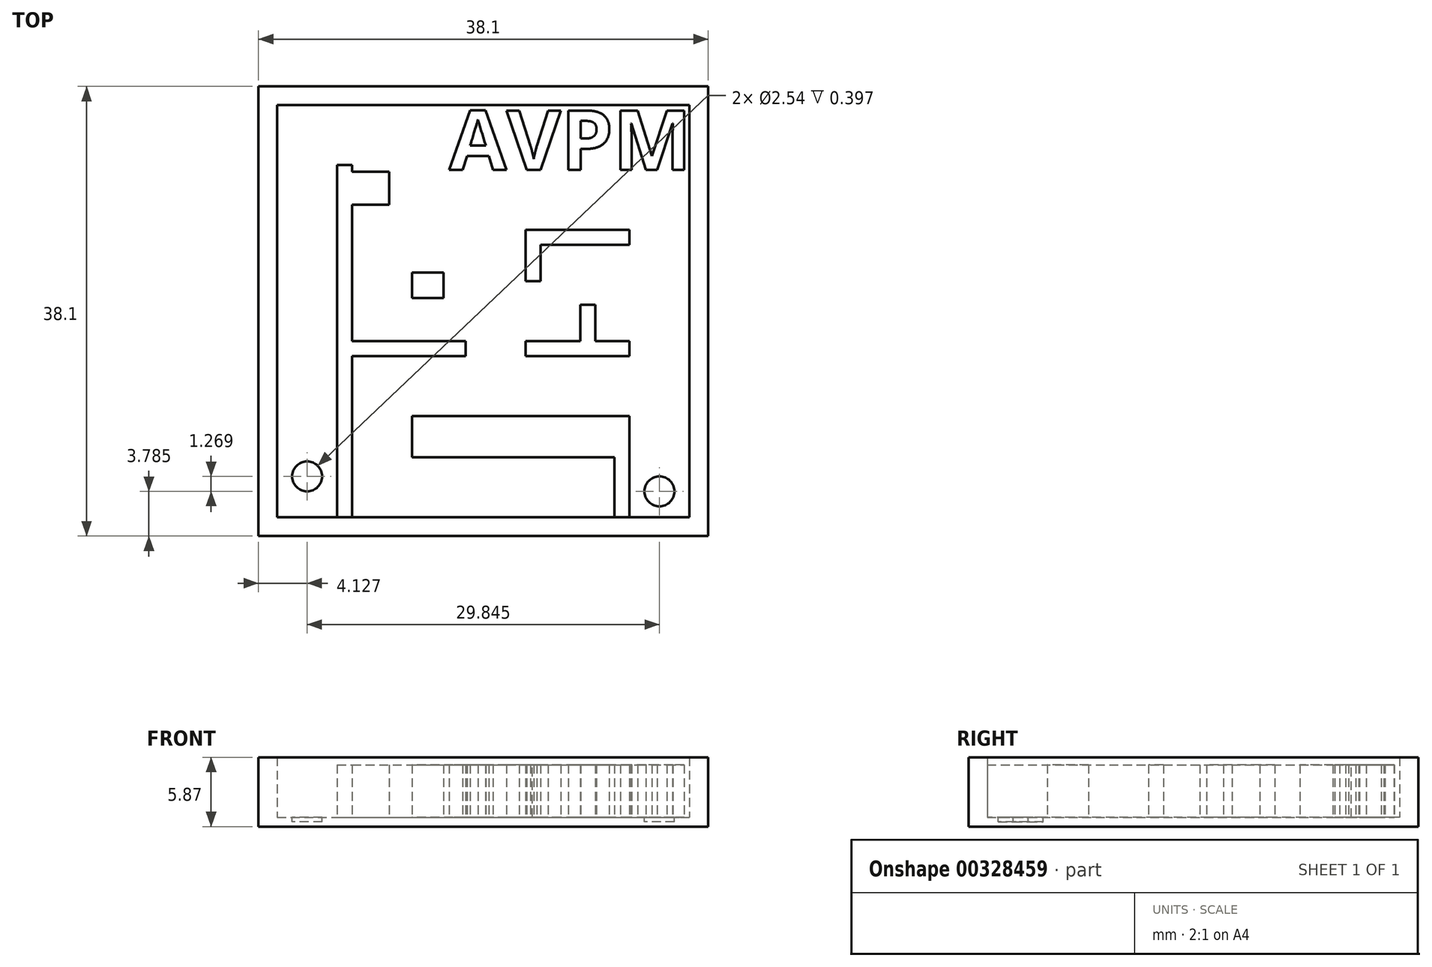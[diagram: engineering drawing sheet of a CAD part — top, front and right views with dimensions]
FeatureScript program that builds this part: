
annotation { "Feature Type Name" : "Feature", "Feature Type Description" : "" }
export const myFeature = defineFeature(function(context is Context, id is Id, definition is map)
    precondition{}
    {
        {
            var Q0;
            Q0=qCreatedBy(makeId("Top.planeOp"),FACE);
            var sketch = newSketch(context, id + "F0", { "sketchPlane" : qUnion([Q0])});
            skLineSegment(sketch, "E0.bottom", {"start": v(-17.86, 15.09) * mm, "end": v(20.24, 15.09) * mm});
            skLineSegment(sketch, "E0.top", {"start": v(-17.86, -23.01) * mm, "end": v(20.24, -23.01) * mm});
            skLineSegment(sketch, "E0.left", {"start": v(-17.86, 15.09) * mm, "end": v(-17.86, -23.01) * mm});
            skLineSegment(sketch, "E0.right", {"start": v(20.24, 15.09) * mm, "end": v(20.24, -23.01) * mm});
            skSolve(sketch);
        }
        {
            var Q0;
            Q0=makeQuery(id+"F0.imprint","IMPRINT",FACE,{"disambiguationData":[TD([[makeQuery(id+"F0.imprint","IMPRINT",EDGE,{"derivedFrom":sQuery(id+"F0.wireOp",EDGE,"E0.bottom")}),-1.0]])]});
            extrude(context, id + "F1", {"entities" : qUnion([Q0]), "depth" : 0.8 * mm});
        }
        {
            var Q0;
            Q0=makeQuery(id+"F1.opExtrude","CAP_FACE",FACE,{"disambiguationData":[OSD([sQuery(id+"F0.wireOp",EDGE,"E0.bottom"),sQuery(id+"F0.wireOp",EDGE,"E0.top"),sQuery(id+"F0.wireOp",EDGE,"E0.left"),sQuery(id+"F0.wireOp",EDGE,"E0.right")])],"isStart":false});
            var sketch = newSketch(context, id + "F2", { "sketchPlane" : qUnion([Q0])});
            skLineSegment(sketch, "E1.0", {"start": v(-16.27, 13.5) * mm, "end": v(18.65, 13.5) * mm});
            skLineSegment(sketch, "E1.1", {"start": v(-16.27, 13.5) * mm, "end": v(-16.27, -21.43) * mm});
            skLineSegment(sketch, "E1.2", {"start": v(-16.27, -21.43) * mm, "end": v(18.65, -21.43) * mm});
            skLineSegment(sketch, "E1.3", {"start": v(18.65, 13.5) * mm, "end": v(18.65, -21.43) * mm});
            skSolve(sketch);
        }
        {
            var Q0;
            Q0=makeQuery(id+"F2.imprint","IMPRINT",FACE,{"disambiguationData":[TD([[makeQuery(id+"F2.imprint","IMPRINT",EDGE,{"derivedFrom":sQuery(id+"F2.wireOp",EDGE,"E1.0")}),1.0]])]});
            extrude(context, id + "F3", {"entities" : qUnion([Q0]), "operationType" : NewBodyOperationType.ADD, "depth" : 5.08 * mm});
        }
        {
            var Q0;
            Q0=makeQuery(id+"F1.opExtrude","CAP_FACE",FACE,{"disambiguationData":[OSD([sQuery(id+"F0.wireOp",EDGE,"E0.bottom"),sQuery(id+"F0.wireOp",EDGE,"E0.top"),sQuery(id+"F0.wireOp",EDGE,"E0.left"),sQuery(id+"F0.wireOp",EDGE,"E0.right")])],"isStart":false});
            var sketch = newSketch(context, id + "F4", { "sketchPlane" : qUnion([Q0])});
            skLineSegment(sketch, "E2.bottom", {"start": v(-11.2, -21.43) * mm, "end": v(-9.92, -21.43) * mm});
            skLineSegment(sketch, "E2.top", {"start": v(-11.2, 8.42) * mm, "end": v(-9.92, 8.42) * mm});
            skLineSegment(sketch, "E2.left", {"start": v(-11.2, -21.43) * mm, "end": v(-11.2, 8.42) * mm});
            skLineSegment(sketch, "E2.right", {"start": v(-9.92, -21.43) * mm, "end": v(-9.92, -7.77) * mm});
            skLineSegment(sketch, "E3.bottom", {"start": v(12.3, -21.43) * mm, "end": v(13.57, -21.43) * mm});
            skLineSegment(sketch, "E3.left", {"start": v(12.3, -21.43) * mm, "end": v(12.3, -16.35) * mm});
            skLineSegment(sketch, "E3.right", {"start": v(13.57, -21.43) * mm, "end": v(13.57, -16.35) * mm});
            skLineSegment(sketch, "E4.bottom", {"start": v(-4.84, -12.85) * mm, "end": v(12.3, -12.85) * mm});
            skLineSegment(sketch, "E4.left", {"start": v(-4.84, -12.85) * mm, "end": v(-4.84, -16.35) * mm});
            skLineSegment(sketch, "E5.right", {"start": v(-0.7, -16.2) * mm, "end": v(-0.7, -16.35) * mm});
            skLineSegment(sketch, "E6.bottom", {"start": v(-9.92, -6.5) * mm, "end": v(-0.3, -6.5) * mm});
            skLineSegment(sketch, "E6.top", {"start": v(-9.92, -7.77) * mm, "end": v(-0.3, -7.77) * mm});
            skLineSegment(sketch, "E6.right", {"start": v(-0.3, -6.5) * mm, "end": v(-0.3, -7.77) * mm});
            skLineSegment(sketch, "E7", {"start": v(-4.84, -16.35) * mm, "end": v(12.3, -16.35) * mm});
            skLineSegment(sketch, "E8.trimOffspring", {"start": v(-9.92, -6.5) * mm, "end": v(-9.92, 5.05) * mm});
            skPoint(sketch, "E9.bottom.end.orphan", {"position": v(0.9, 4.03) * mm});
            skPoint(sketch, "E10.right.end.orphan", {"position": v(-4.84, -1.05) * mm});
            skPoint(sketch, "E11.trimOffspring.start.orphan", {"position": v(0.9, -2.32) * mm});
            skPoint(sketch, "E12.top.start.orphan", {"position": v(0.9, -8.68) * mm});
            skPoint(sketch, "E9.right.start.orphan", {"position": v(13.78, 4.03) * mm});
            skLineSegment(sketch, "E13.bottom", {"start": v(4.78, 2.93) * mm, "end": v(13.57, 2.93) * mm});
            skLineSegment(sketch, "E13.top", {"start": v(4.78, -7.77) * mm, "end": v(13.57, -7.77) * mm});
            skLineSegment(sketch, "E13.left", {"start": v(4.78, 2.93) * mm, "end": v(4.78, 1.66) * mm});
            skLineSegment(sketch, "E13.right", {"start": v(13.57, 2.93) * mm, "end": v(13.57, 1.66) * mm});
            skLineSegment(sketch, "E14.bottom", {"start": v(4.78, -6.5) * mm, "end": v(9.4, -6.5) * mm});
            skLineSegment(sketch, "E14.top", {"start": v(4.78, 1.66) * mm, "end": v(4.79, 1.66) * mm});
            skLineSegment(sketch, "E15.trimOffspring", {"start": v(13.57, -6.5) * mm, "end": v(13.57, -7.77) * mm});
            skLineSegment(sketch, "E16.trimOffspring", {"start": v(4.78, -6.5) * mm, "end": v(4.78, -7.77) * mm});
            skLineSegment(sketch, "E17.top", {"start": v(4.79, -1.42) * mm, "end": v(6.06, -1.42) * mm});
            skLineSegment(sketch, "E17.left", {"start": v(4.79, 1.66) * mm, "end": v(4.79, -1.42) * mm});
            skLineSegment(sketch, "E17.right", {"start": v(6.06, 1.66) * mm, "end": v(6.06, -1.42) * mm});
            skLineSegment(sketch, "E18.top", {"start": v(10.68, -3.42) * mm, "end": v(9.4, -3.42) * mm});
            skLineSegment(sketch, "E18.left", {"start": v(10.68, -6.5) * mm, "end": v(10.68, -3.42) * mm});
            skLineSegment(sketch, "E18.right", {"start": v(9.4, -6.5) * mm, "end": v(9.4, -3.42) * mm});
            skText(sketch, "E19", { "text": "AVPM", "fontName": "OpenSans-Bold.ttf"});
            skLineSegment(sketch, "E20", {"start": v(-11.2, -21.43) * mm, "end": v(-16.27, -21.43) * mm});
            skCircle(sketch, "E21", {"center": v(-13.73, -17.96) * mm, "radius": 1.27 * mm});
            skPoint(sketch, "E21.centerSnap0", {"position": v(-13.73, -21.43) * mm});
            skLineSegment(sketch, "E22", {"start": v(13.57, -21.43) * mm, "end": v(18.65, -21.43) * mm});
            skCircle(sketch, "E23", {"center": v(16.11, -19.23) * mm, "radius": 1.27 * mm});
            skPoint(sketch, "E23.centerSnap0", {"position": v(16.11, -21.43) * mm});
            skLineSegment(sketch, "E24.trimOffspring", {"start": v(10.68, -6.5) * mm, "end": v(13.57, -6.5) * mm});
            skLineSegment(sketch, "E25.trimOffspring", {"start": v(6.06, 1.66) * mm, "end": v(13.57, 1.66) * mm});
            skLineSegment(sketch, "E26", {"start": v(13.57, -16.35) * mm, "end": v(13.57, -12.85) * mm});
            skLineSegment(sketch, "E27", {"start": v(13.57, -12.85) * mm, "end": v(12.3, -12.85) * mm});
            skPoint(sketch, "E28.centerSnap0", {"position": v(-9.92, 0.96) * mm});
            skPoint(sketch, "E28.center.orphan", {"position": v(-2.57, 0.96) * mm});
            skLineSegment(sketch, "E29.bottom", {"start": v(-4.84, -0.69) * mm, "end": v(-2.17, -0.69) * mm});
            skLineSegment(sketch, "E29.top", {"start": v(-4.84, -2.84) * mm, "end": v(-2.17, -2.84) * mm});
            skLineSegment(sketch, "E29.left", {"start": v(-4.84, -0.69) * mm, "end": v(-4.84, -2.84) * mm});
            skLineSegment(sketch, "E29.right", {"start": v(-2.17, -0.69) * mm, "end": v(-2.17, -2.84) * mm});
            skLineSegment(sketch, "E30.bottom", {"start": v(-9.95, 7.86) * mm, "end": v(-6.79, 7.86) * mm});
            skLineSegment(sketch, "E30.top", {"start": v(-9.95, 5.05) * mm, "end": v(-6.79, 5.05) * mm});
            skLineSegment(sketch, "E30.right", {"start": v(-6.79, 7.86) * mm, "end": v(-6.79, 5.05) * mm});
            skLineSegment(sketch, "E31.trimOffspring", {"start": v(-9.92, 7.86) * mm, "end": v(-9.92, 8.42) * mm});
            const initialGuessF4  = {"E19": [-0.0017, 0.008, 1, 0, 0.00508]};
            skSetInitialGuess(sketch, initialGuessF4);
            skSolve(sketch);
        }
        {
            var Q0;
            Q0=makeQuery(id+"F4.imprint","IMPRINT",FACE,{"disambiguationData":[TD([[makeQuery(id+"F4.imprint","IMPRINT",EDGE,{"derivedFrom":sQuery(id+"F4.wireOp",EDGE,"E21")}),1.0]])]});
            var Q1;
            Q1=makeQuery(id+"F4.imprint","IMPRINT",FACE,{"disambiguationData":[TD([[makeQuery(id+"F4.imprint","IMPRINT",EDGE,{"derivedFrom":sQuery(id+"F4.wireOp",EDGE,"E23")}),1.0]])]});
            extrude(context, id + "F5", {"entities" : qUnion([Q0, Q1]), "operationType" : NewBodyOperationType.REMOVE, "oppositeDirection" : true, "depth" : 0.4 * mm});
        }
        {
            var Q0;
            Q0=makeQuery(id+"F4.imprint","IMPRINT",FACE,{"disambiguationData":[TD([[makeQuery(id+"F4.imprint","IMPRINT",EDGE,{"derivedFrom":sQuery(id+"F4.wireOp",EDGE,"E2.bottom")}),1.0]])]});
            var Q1;
            Q1=makeQuery(id+"F4.imprint","IMPRINT",FACE,{"disambiguationData":[TD([[makeQuery(id+"F4.imprint","IMPRINT",EDGE,{"derivedFrom":sQuery(id+"F4.wireOp",EDGE,"E13.top")}),1.0]])]});
            var Q2;
            Q2=makeQuery(id+"F4.imprint","IMPRINT",FACE,{"disambiguationData":[TD([[makeQuery(id+"F4.imprint","IMPRINT",EDGE,{"derivedFrom":sQuery(id+"F4.wireOp",EDGE,"E13.bottom")}),-1.0]])]});
            var Q3;
            Q3=makeQuery(id+"F4.imprint","IMPRINT",FACE,{"disambiguationData":[TD([[makeQuery(id+"F4.imprint","IMPRINT",EDGE,{"derivedFrom":sQuery(id+"F4.wireOp",EDGE,"nkdr1mb9-7Me6-TDAS-JZjQ-Xdjvqa2YZYCh.top")}),1.0]])]});
            var Q4;
            Q4=makeQuery(id+"F4.imprint","IMPRINT",FACE,{"disambiguationData":[TD([[makeQuery(id+"F4.imprint","IMPRINT",EDGE,{"derivedFrom":sQuery(id+"F4.wireOp",EDGE,"E4.bottom")}),-1.0]])]});
            extrude(context, id + "F6", {"entities" : qUnion([Q0, Q1, Q2, Q3, Q4]), "operationType" : NewBodyOperationType.ADD, "depth" : 4.44 * mm});
        }
        {
            var Q0;
            Q0=makeQuery(id+"F4.imprint","IMPRINT",FACE,{"disambiguationData":[TD([[makeQuery(id+"F4.imprint","IMPRINT",EDGE,{"derivedFrom":sQuery(id+"F4.wireOp",EDGE,"E19.sketch_text.stroke-0")}),-1.0]])]});
            var Q1;
            Q1=makeQuery(id+"F4.imprint","IMPRINT",FACE,{"disambiguationData":[TD([[makeQuery(id+"F4.imprint","IMPRINT",EDGE,{"derivedFrom":sQuery(id+"F4.wireOp",EDGE,"E19.sketch_text.stroke-38")}),-1.0]])]});
            var Q2;
            Q2=makeQuery(id+"F4.imprint","IMPRINT",FACE,{"disambiguationData":[TD([[makeQuery(id+"F4.imprint","IMPRINT",EDGE,{"derivedFrom":sQuery(id+"F4.wireOp",EDGE,"E19.sketch_text.stroke-22")}),-1.0]])]});
            var Q3;
            Q3=makeQuery(id+"F4.imprint","IMPRINT",FACE,{"disambiguationData":[TD([[makeQuery(id+"F4.imprint","IMPRINT",EDGE,{"derivedFrom":sQuery(id+"F4.wireOp",EDGE,"E19.sketch_text.stroke-12")}),-1.0]])]});
            extrude(context, id + "F7", {"entities" : qUnion([Q0, Q1, Q2, Q3]), "operationType" : NewBodyOperationType.ADD, "depth" : 4.44 * mm});
        }
        {
            var Q0;
            Q0=makeQuery(id+"F4.imprint","IMPRINT",FACE,{"disambiguationData":[TD([[makeQuery(id+"F4.imprint","IMPRINT",EDGE,{"derivedFrom":sQuery(id+"F4.wireOp",EDGE,"E29.bottom")}),-1.0]])]});
            extrude(context, id + "F8", {"entities" : qUnion([Q0]), "operationType" : NewBodyOperationType.ADD, "depth" : 4.44 * mm});
        }
    });
